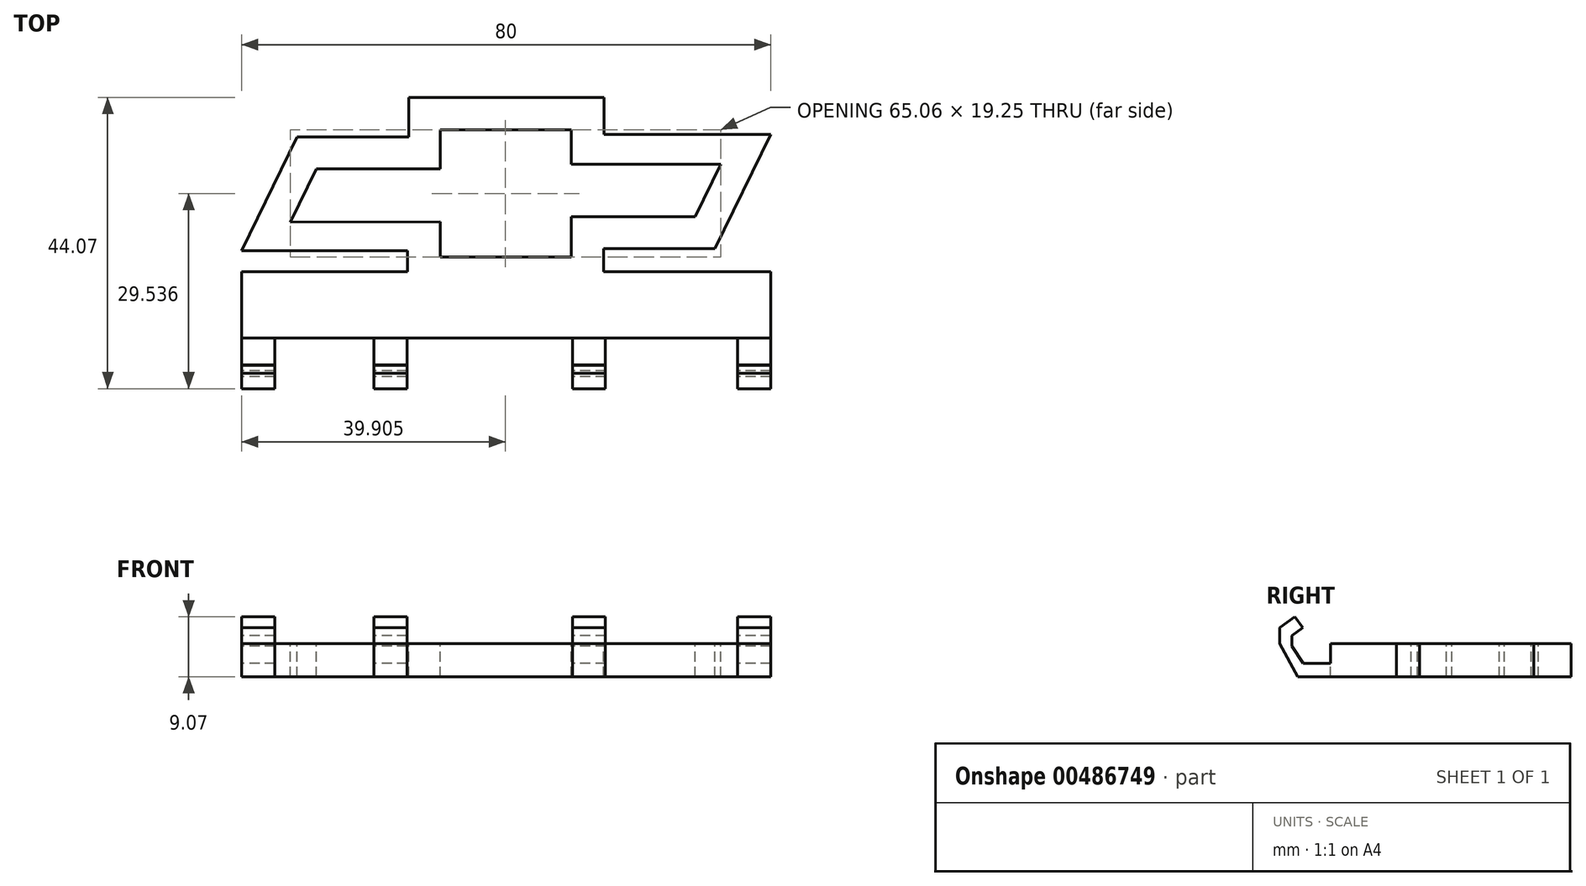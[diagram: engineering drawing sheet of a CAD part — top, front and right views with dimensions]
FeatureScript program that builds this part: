
annotation { "Feature Type Name" : "Feature", "Feature Type Description" : "" }
export const myFeature = defineFeature(function(context is Context, id is Id, definition is map)
    precondition{}
    {
        {
            var Q0;
            Q0=qCreatedBy(makeId("Top.planeOp"),FACE);
            var sketch = newSketch(context, id + "F0", { "sketchPlane" : qUnion([Q0])});
            skLineSegment(sketch, "E0.bottom", {"start": v(0, 0) * mm, "end": v(80, 0) * mm});
            skLineSegment(sketch, "E0.top", {"start": v(0, 10) * mm, "end": v(80, 10) * mm});
            skLineSegment(sketch, "E0.left", {"start": v(0, 0) * mm, "end": v(0, 10) * mm});
            skLineSegment(sketch, "E0.right", {"start": v(80, 0) * mm, "end": v(80, 10) * mm});
            skSolve(sketch);
        }
        {
            var Q0;
            Q0 = qSketchRegion(id + "F0", true);
            extrude(context, id + "F1", {"entities" : qUnion([Q0]), "depth" : 5 * mm});
        }
        {
            var Q0;
            Q0=qCreatedBy(makeId("Right.planeOp"),FACE);
            var sketch = newSketch(context, id + "F2", { "sketchPlane" : qUnion([Q0])});
            skLineSegment(sketch, "E1", {"start": v(0, 0) * mm, "end": v(-4.96, 0) * mm});
            skLineSegment(sketch, "E2", {"start": v(-4.96, 0) * mm, "end": v(-7.69, 5.02) * mm});
            skLineSegment(sketch, "E3", {"start": v(-7.69, 5.02) * mm, "end": v(-7.69, 7.41) * mm});
            skLineSegment(sketch, "E4", {"start": v(-7.69, 7.41) * mm, "end": v(-5.36, 9.07) * mm});
            skLineSegment(sketch, "E5", {"start": v(-5.36, 9.07) * mm, "end": v(-4.17, 7.41) * mm});
            skLineSegment(sketch, "E6", {"start": v(-4.17, 7.41) * mm, "end": v(-5.84, 6.22) * mm});
            skLineSegment(sketch, "E7", {"start": v(-5.84, 6.22) * mm, "end": v(-5.84, 4.62) * mm});
            skLineSegment(sketch, "E8", {"start": v(-5.84, 4.62) * mm, "end": v(-4.1, 2.03) * mm});
            skLineSegment(sketch, "E9", {"start": v(-4.1, 2.03) * mm, "end": v(0, 2.03) * mm});
            skLineSegment(sketch, "E10", {"start": v(0, 2.03) * mm, "end": v(0, 0) * mm});
            skSolve(sketch);
        }
        {
            var Q0;
            Q0 = qSketchRegion(id + "F2", true);
            extrude(context, id + "F3", {"entities" : qUnion([Q0]), "operationType" : NewBodyOperationType.ADD, "depth" : 5 * mm});
        }
        {
            var Q0;
            Q0=makeQuery(id+"F3.opExtrude","CAP_FACE",FACE,{"disambiguationData":[OSD([sQuery(id+"F2.wireOp",EDGE,"E1"),sQuery(id+"F2.wireOp",EDGE,"E2"),sQuery(id+"F2.wireOp",EDGE,"E3"),sQuery(id+"F2.wireOp",EDGE,"E4"),sQuery(id+"F2.wireOp",EDGE,"E5"),sQuery(id+"F2.wireOp",EDGE,"E6"),sQuery(id+"F2.wireOp",EDGE,"E7"),sQuery(id+"F2.wireOp",EDGE,"E8"),sQuery(id+"F2.wireOp",EDGE,"E9"),sQuery(id+"F2.wireOp",EDGE,"E10")])],"isStart":false});
            cPlane(context, id + "F4", {"entities" : qUnion([Q0]), "cplaneType" : CPlaneType.OFFSET, "offset" : 15 * mm, "width" : 150 * mm, "height" : 150 * mm});
        }
        {
            var Q0;
            Q0=qCreatedBy(id+"F4.planeOp",FACE);
            var sketch = newSketch(context, id + "F5", { "sketchPlane" : qUnion([Q0])});
            skLineSegment(sketch, "E11.0.0", {"start": v(0, 0) * mm, "end": v(0, 2.03) * mm});
            skLineSegment(sketch, "E11.0.1", {"start": v(0, 2.03) * mm, "end": v(-4.1, 2.03) * mm});
            skLineSegment(sketch, "E11.0.2", {"start": v(-4.1, 2.03) * mm, "end": v(-5.84, 4.62) * mm});
            skLineSegment(sketch, "E11.0.3", {"start": v(-5.84, 4.62) * mm, "end": v(-5.84, 6.22) * mm});
            skLineSegment(sketch, "E11.0.4", {"start": v(-5.84, 6.22) * mm, "end": v(-4.17, 7.41) * mm});
            skLineSegment(sketch, "E11.0.5", {"start": v(-4.17, 7.41) * mm, "end": v(-5.36, 9.07) * mm});
            skLineSegment(sketch, "E11.0.6", {"start": v(-5.36, 9.07) * mm, "end": v(-7.69, 7.41) * mm});
            skLineSegment(sketch, "E11.0.7", {"start": v(-7.69, 7.41) * mm, "end": v(-7.69, 5.02) * mm});
            skLineSegment(sketch, "E11.0.8", {"start": v(-7.69, 5.02) * mm, "end": v(-4.96, 0) * mm});
            skLineSegment(sketch, "E11.0.9", {"start": v(-4.96, 0) * mm, "end": v(0, 0) * mm});
            skLineSegment(sketch, "E12", {"start": v(-5.36, 9.07) * mm, "end": v(-4.17, 7.41) * mm});
            skSolve(sketch);
        }
        {
            var Q0;
            Q0=makeQuery(id+"F5.imprint","IMPRINT",FACE,{"disambiguationData":[TD([[makeQuery(id+"F5.imprint","IMPRINT",EDGE,{"derivedFrom":sQuery(id+"F5.wireOp",EDGE,"E11.0.0")}),1.0]])]});
            extrude(context, id + "F6", {"entities" : qUnion([Q0]), "operationType" : NewBodyOperationType.ADD, "depth" : 5 * mm});
        }
        {
            var Q0;
            Q0=makeQuery(id+"F6.opExtrude","CAP_FACE",FACE,{"disambiguationData":[OSD([sQuery(id+"F5.wireOp",EDGE,"E11.0.0"),sQuery(id+"F5.wireOp",EDGE,"E11.0.1"),sQuery(id+"F5.wireOp",EDGE,"E11.0.2"),sQuery(id+"F5.wireOp",EDGE,"E11.0.3"),sQuery(id+"F5.wireOp",EDGE,"E11.0.4"),sQuery(id+"F5.wireOp",EDGE,"E11.0.6"),sQuery(id+"F5.wireOp",EDGE,"E11.0.7"),sQuery(id+"F5.wireOp",EDGE,"E11.0.8"),sQuery(id+"F5.wireOp",EDGE,"E11.0.9"),sQuery(id+"F5.wireOp",EDGE,"E12")])],"isStart":false});
            cPlane(context, id + "F7", {"entities" : qUnion([Q0]), "cplaneType" : CPlaneType.OFFSET, "offset" : 25 * mm, "width" : 150 * mm, "height" : 150 * mm});
        }
        {
            var Q0;
            Q0=qCreatedBy(id+"F7.planeOp",FACE);
            var sketch = newSketch(context, id + "F8", { "sketchPlane" : qUnion([Q0])});
            skLineSegment(sketch, "E13.0.0", {"start": v(-7.69, 7.41) * mm, "end": v(-7.69, 5.02) * mm});
            skLineSegment(sketch, "E13.0.1", {"start": v(-7.69, 5.02) * mm, "end": v(-4.96, 0) * mm});
            skLineSegment(sketch, "E13.0.2", {"start": v(-4.96, 0) * mm, "end": v(0, 0) * mm});
            skLineSegment(sketch, "E13.0.3", {"start": v(0, 0) * mm, "end": v(0, 2.03) * mm});
            skLineSegment(sketch, "E13.0.4", {"start": v(0, 2.03) * mm, "end": v(-4.1, 2.03) * mm});
            skLineSegment(sketch, "E13.0.5", {"start": v(-4.1, 2.03) * mm, "end": v(-5.84, 4.62) * mm});
            skLineSegment(sketch, "E13.0.6", {"start": v(-5.84, 4.62) * mm, "end": v(-5.84, 6.22) * mm});
            skLineSegment(sketch, "E13.0.7", {"start": v(-5.84, 6.22) * mm, "end": v(-4.17, 7.41) * mm});
            skLineSegment(sketch, "E13.0.8", {"start": v(-4.17, 7.41) * mm, "end": v(-5.36, 9.07) * mm});
            skLineSegment(sketch, "E13.0.9", {"start": v(-5.36, 9.07) * mm, "end": v(-7.69, 7.41) * mm});
            skSolve(sketch);
        }
        {
            var Q0;
            Q0 = qSketchRegion(id + "F8", true);
            extrude(context, id + "F9", {"entities" : qUnion([Q0]), "operationType" : NewBodyOperationType.ADD, "depth" : 5 * mm});
        }
        {
            var Q0;
            Q0=makeQuery(id+"F9.opExtrude","CAP_FACE",FACE,{"disambiguationData":[OSD([sQuery(id+"F8.wireOp",EDGE,"E13.0.0"),sQuery(id+"F8.wireOp",EDGE,"E13.0.1"),sQuery(id+"F8.wireOp",EDGE,"E13.0.2"),sQuery(id+"F8.wireOp",EDGE,"E13.0.3"),sQuery(id+"F8.wireOp",EDGE,"E13.0.4"),sQuery(id+"F8.wireOp",EDGE,"E13.0.5"),sQuery(id+"F8.wireOp",EDGE,"E13.0.6"),sQuery(id+"F8.wireOp",EDGE,"E13.0.7"),sQuery(id+"F8.wireOp",EDGE,"E13.0.8"),sQuery(id+"F8.wireOp",EDGE,"E13.0.9")])],"isStart":false});
            cPlane(context, id + "F10", {"entities" : qUnion([Q0]), "cplaneType" : CPlaneType.OFFSET, "offset" : 20 * mm, "width" : 150 * mm, "height" : 150 * mm});
        }
        {
            var Q0;
            Q0=qCreatedBy(id+"F10.planeOp",FACE);
            var sketch = newSketch(context, id + "F11", { "sketchPlane" : qUnion([Q0])});
            skLineSegment(sketch, "E14.0.0", {"start": v(-4.17, 7.41) * mm, "end": v(-5.36, 9.07) * mm});
            skLineSegment(sketch, "E14.0.1", {"start": v(-5.36, 9.07) * mm, "end": v(-7.69, 7.41) * mm});
            skLineSegment(sketch, "E14.0.2", {"start": v(-7.69, 7.41) * mm, "end": v(-7.69, 5.02) * mm});
            skLineSegment(sketch, "E14.0.3", {"start": v(-7.69, 5.02) * mm, "end": v(-4.96, 0) * mm});
            skLineSegment(sketch, "E14.0.4", {"start": v(-4.96, 0) * mm, "end": v(0, 0) * mm});
            skLineSegment(sketch, "E14.0.5", {"start": v(0, 0) * mm, "end": v(0, 2.03) * mm});
            skLineSegment(sketch, "E14.0.6", {"start": v(0, 2.03) * mm, "end": v(-4.1, 2.03) * mm});
            skLineSegment(sketch, "E14.0.7", {"start": v(-4.1, 2.03) * mm, "end": v(-5.84, 4.62) * mm});
            skLineSegment(sketch, "E14.0.8", {"start": v(-5.84, 4.62) * mm, "end": v(-5.84, 6.22) * mm});
            skLineSegment(sketch, "E14.0.9", {"start": v(-5.84, 6.22) * mm, "end": v(-4.17, 7.41) * mm});
            skSolve(sketch);
        }
        {
            var Q0;
            Q0 = qSketchRegion(id + "F11", true);
            extrude(context, id + "F12", {"entities" : qUnion([Q0]), "operationType" : NewBodyOperationType.ADD, "depth" : 5 * mm});
        }
        {
            var Q0;
            Q0=makeQuery(id+"F1.opExtrude","CAP_FACE",FACE,{"disambiguationData":[OSD([sQuery(id+"F0.wireOp",EDGE,"E0.bottom"),sQuery(id+"F0.wireOp",EDGE,"E0.top"),sQuery(id+"F0.wireOp",EDGE,"E0.left"),sQuery(id+"F0.wireOp",EDGE,"E0.right")])],"isStart":false});
            var sketch = newSketch(context, id + "F13", { "sketchPlane" : qUnion([Q0])});
            skLineSegment(sketch, "E15", {"start": v(0, 13.17) * mm, "end": v(8.39, 30.37) * mm});
            skLineSegment(sketch, "E16", {"start": v(8.39, 30.37) * mm, "end": v(25.25, 30.37) * mm});
            skLineSegment(sketch, "E17", {"start": v(25.25, 30.37) * mm, "end": v(25.25, 36.38) * mm});
            skLineSegment(sketch, "E18", {"start": v(25.25, 36.38) * mm, "end": v(54.8, 36.38) * mm});
            skLineSegment(sketch, "E19", {"start": v(54.8, 36.38) * mm, "end": v(54.8, 30.76) * mm});
            skLineSegment(sketch, "E20", {"start": v(54.8, 30.76) * mm, "end": v(80, 30.76) * mm});
            skLineSegment(sketch, "E21", {"start": v(80, 30.76) * mm, "end": v(71.58, 13.5) * mm});
            skLineSegment(sketch, "E22", {"start": v(71.58, 13.5) * mm, "end": v(54.73, 13.5) * mm});
            skLineSegment(sketch, "E23", {"start": v(54.73, 13.5) * mm, "end": v(54.73, 7.49) * mm});
            skLineSegment(sketch, "E24", {"start": v(54.73, 7.49) * mm, "end": v(25.1, 7.49) * mm});
            skLineSegment(sketch, "E25", {"start": v(25.1, 7.49) * mm, "end": v(25.1, 13.2) * mm});
            skLineSegment(sketch, "E26", {"start": v(25.1, 13.2) * mm, "end": v(0, 13.17) * mm});
            skLineSegment(sketch, "E27", {"start": v(7.38, 17.53) * mm, "end": v(11.27, 25.57) * mm});
            skLineSegment(sketch, "E28", {"start": v(11.27, 25.57) * mm, "end": v(30.02, 25.57) * mm});
            skLineSegment(sketch, "E29", {"start": v(30.02, 25.57) * mm, "end": v(30.02, 31.47) * mm});
            skLineSegment(sketch, "E30", {"start": v(30.02, 31.47) * mm, "end": v(49.85, 31.47) * mm});
            skLineSegment(sketch, "E31", {"start": v(49.85, 31.47) * mm, "end": v(49.85, 26.3) * mm});
            skLineSegment(sketch, "E32", {"start": v(49.85, 26.3) * mm, "end": v(72.43, 26.3) * mm});
            skLineSegment(sketch, "E33", {"start": v(72.43, 26.3) * mm, "end": v(68.58, 18.35) * mm});
            skLineSegment(sketch, "E34", {"start": v(68.58, 18.35) * mm, "end": v(49.85, 18.35) * mm});
            skLineSegment(sketch, "E35", {"start": v(49.85, 18.35) * mm, "end": v(49.85, 12.22) * mm});
            skLineSegment(sketch, "E36", {"start": v(49.85, 12.22) * mm, "end": v(30.02, 12.22) * mm});
            skLineSegment(sketch, "E37", {"start": v(30.02, 12.22) * mm, "end": v(30.02, 17.56) * mm});
            skLineSegment(sketch, "E38", {"start": v(30.02, 17.56) * mm, "end": v(7.38, 17.53) * mm});
            skSolve(sketch);
        }
        {
            var Q0;
            Q0=makeQuery(id+"F13.imprint","IMPRINT",FACE,{"disambiguationData":[TD([[makeQuery(id+"F13.imprint","IMPRINT",EDGE,{"derivedFrom":sQuery(id+"F13.wireOp",EDGE,"E15")}),-1.0]])]});
            extrude(context, id + "F14", {"entities" : qUnion([Q0]), "operationType" : NewBodyOperationType.ADD, "oppositeDirection" : true, "depth" : 5 * mm});
        }
    });
